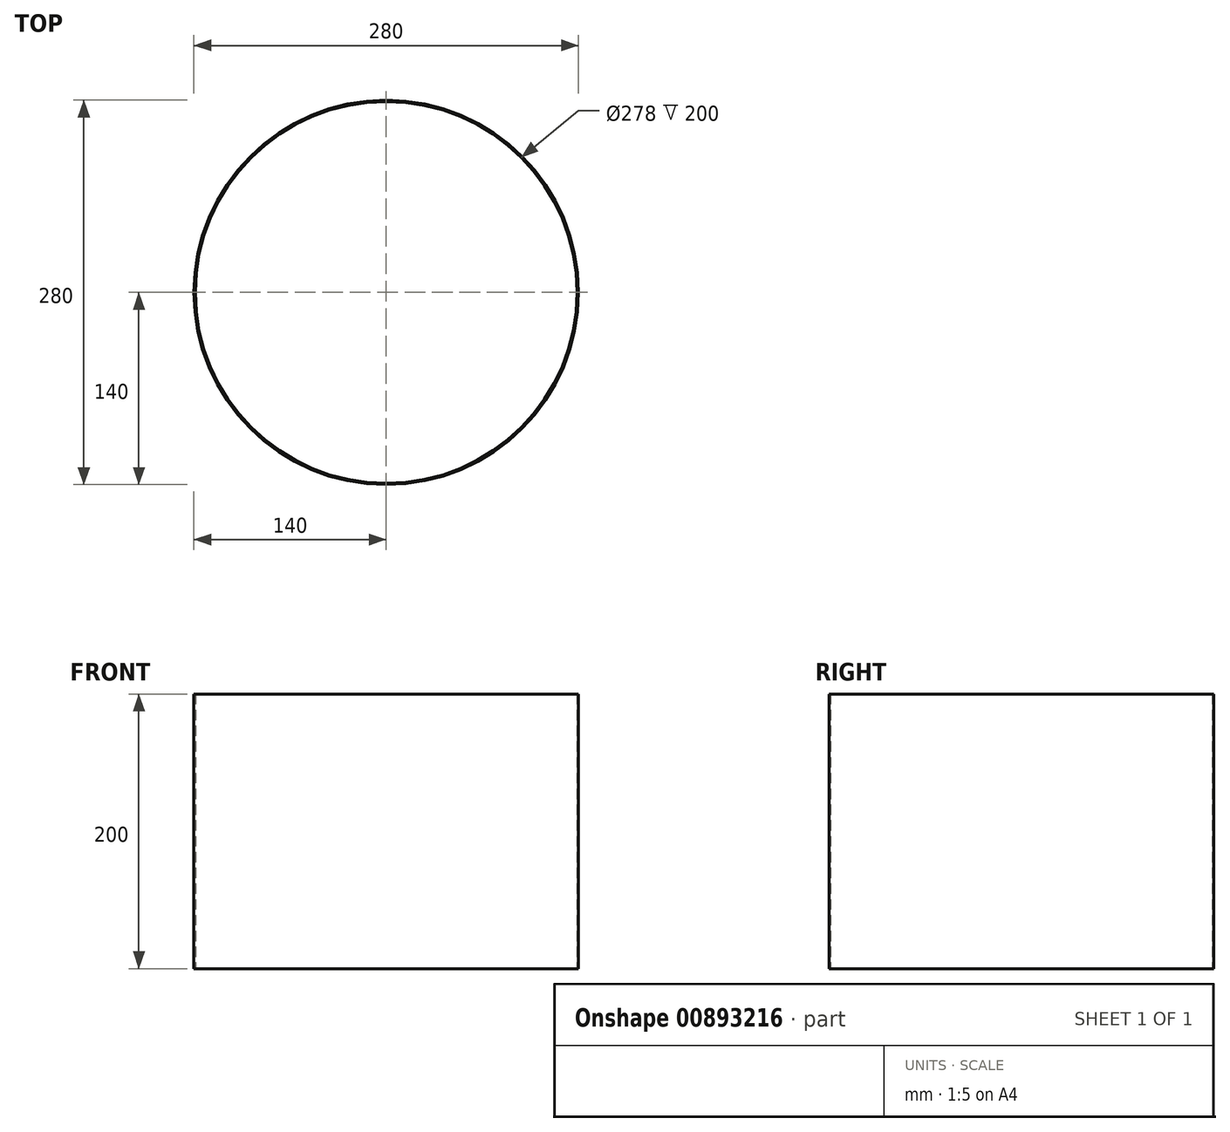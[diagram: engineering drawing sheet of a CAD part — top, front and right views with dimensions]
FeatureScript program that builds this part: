
annotation { "Feature Type Name" : "Feature", "Feature Type Description" : "" }
export const myFeature = defineFeature(function(context is Context, id is Id, definition is map)
    precondition{}
    {
        {
            var Q0;
            Q0=qCreatedBy(makeId("Top.planeOp"),FACE);
            var sketch = newSketch(context, id + "F0", { "sketchPlane" : qUnion([Q0])});
            skCircle(sketch, "E0", {"center": v(0, 0) * mm, "radius": 139 * mm});
            skCircle(sketch, "E1", {"center": v(0, 0) * mm, "radius": 140 * mm});
            skSolve(sketch);
        }
        {
            var Q0;
            Q0=makeQuery(id+"F0.imprint","IMPRINT",FACE,{"disambiguationData":[TD([[makeQuery(id+"F0.imprint","IMPRINT",EDGE,{"derivedFrom":sQuery(id+"F0.wireOp",EDGE,"E0")}),-1.0]])]});
            extrude(context, id + "F1", {"entities" : qUnion([Q0]), "depth" : 200 * mm, "offsetDistance" : 25 * mm});
        }
    });
